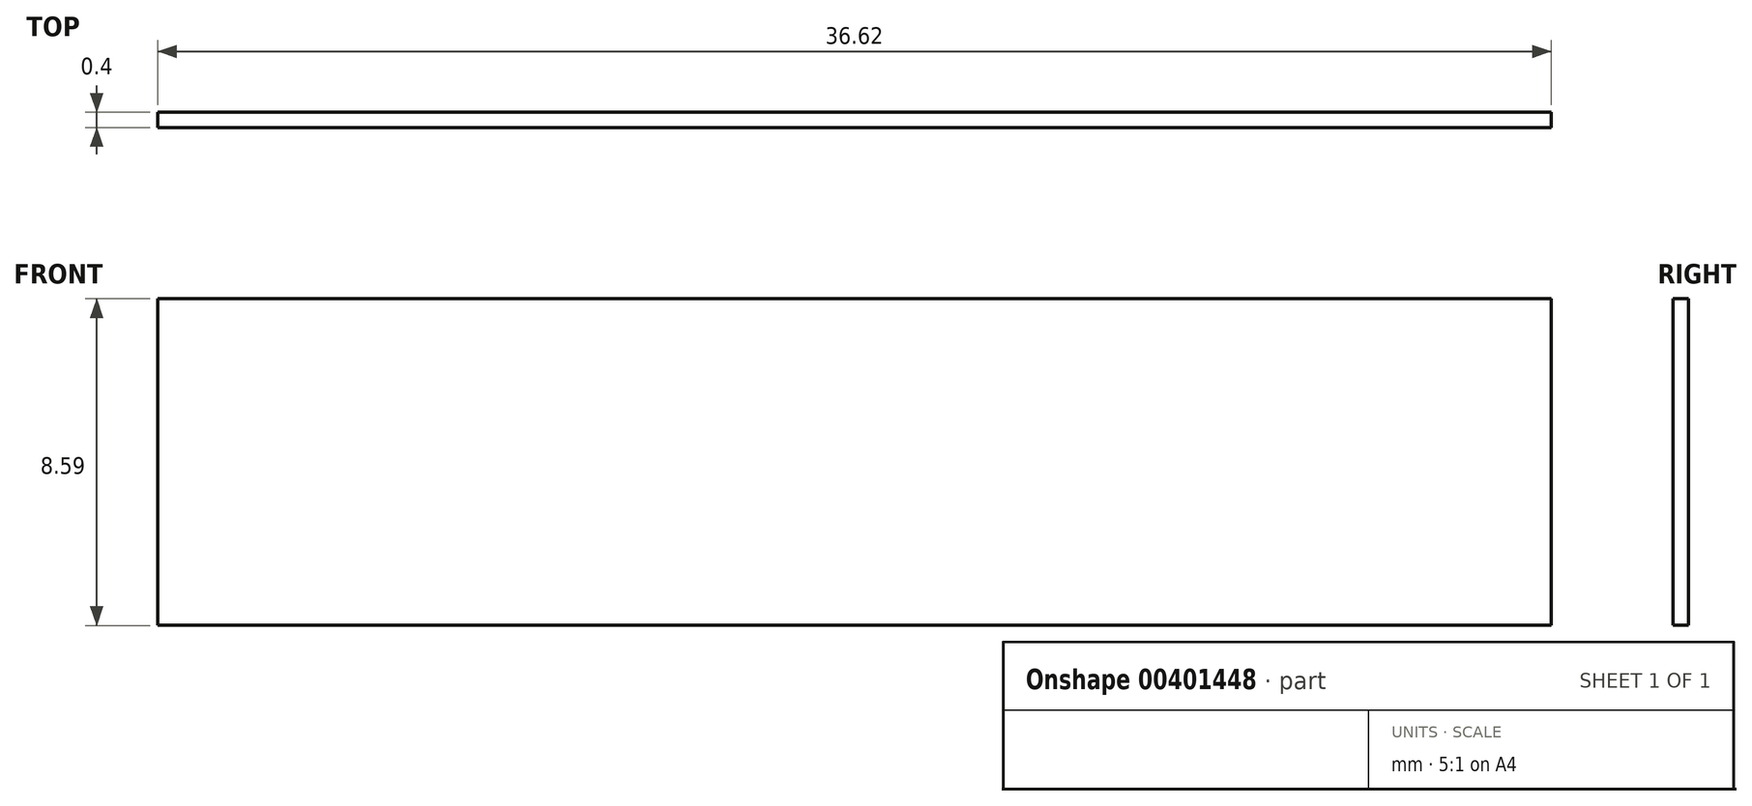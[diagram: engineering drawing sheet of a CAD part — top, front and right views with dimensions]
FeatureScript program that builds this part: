
annotation { "Feature Type Name" : "Feature", "Feature Type Description" : "" }
export const myFeature = defineFeature(function(context is Context, id is Id, definition is map)
    precondition{}
    {
        {
            var Q0;
            Q0=qCreatedBy(makeId("Front.planeOp"),FACE);
            var sketch = newSketch(context, id + "F0", { "sketchPlane" : qUnion([Q0])});
            skLineSegment(sketch, "E0.bottom", {"start": v(-96.57, 56.74) * mm, "end": v(-45.77, 56.74) * mm});
            skLineSegment(sketch, "E0.top", {"start": v(-96.57, 36.3) * mm, "end": v(-45.77, 36.3) * mm});
            skLineSegment(sketch, "E0.left", {"start": v(-96.57, 56.74) * mm, "end": v(-96.57, 36.3) * mm});
            skLineSegment(sketch, "E0.right", {"start": v(-45.77, 56.74) * mm, "end": v(-45.77, 36.3) * mm});
            skSolve(sketch);
        }
        {
            var Q0;
            Q0=makeQuery(id+"F0.imprint","IMPRINT",FACE,{"disambiguationData":[TD([[makeQuery(id+"F0.imprint","IMPRINT",EDGE,{"derivedFrom":sQuery(id+"F0.wireOp",EDGE,"E0.bottom")}),-1.0]])]});
            extrude(context, id + "F1", {"entities" : qUnion([Q0]), "depth" : 1.42 * mm});
        }
        {
            var Q0;
            Q0=qCreatedBy(makeId("Front.planeOp"),FACE);
            var sketch = newSketch(context, id + "F2", { "sketchPlane" : qUnion([Q0])});
            skLineSegment(sketch, "E1.bottom", {"start": v(-111.71, 21.03) * mm, "end": v(-52.05, 21.03) * mm});
            skLineSegment(sketch, "E1.top", {"start": v(-111.71, 5.53) * mm, "end": v(-52.05, 5.53) * mm});
            skLineSegment(sketch, "E1.left", {"start": v(-111.71, 21.03) * mm, "end": v(-111.71, 5.53) * mm});
            skLineSegment(sketch, "E1.right", {"start": v(-52.05, 21.03) * mm, "end": v(-52.05, 5.53) * mm});
            skLineSegment(sketch, "E2.bottom", {"start": v(-110.8, 20.06) * mm, "end": v(-53.17, 20.06) * mm});
            skLineSegment(sketch, "E2.top", {"start": v(-110.8, 6.7) * mm, "end": v(-53.17, 6.7) * mm});
            skLineSegment(sketch, "E2.left", {"start": v(-110.8, 20.06) * mm, "end": v(-110.8, 6.7) * mm});
            skLineSegment(sketch, "E2.right", {"start": v(-53.17, 20.06) * mm, "end": v(-53.17, 6.7) * mm});
            skSolve(sketch);
        }
        {
            var Q0;
            Q0=makeQuery(id+"F2.imprint","IMPRINT",FACE,{"disambiguationData":[TD([[makeQuery(id+"F2.imprint","IMPRINT",EDGE,{"derivedFrom":sQuery(id+"F2.wireOp",EDGE,"E1.bottom")}),-1.0]])]});
            extrude(context, id + "F3", {"entities" : qUnion([Q0]), "depth" : 25.4 * mm});
        }
        {
            var Q0;
            Q0=makeQuery(id+"F3.opExtrude","SWEPT_BODY",BODY,{"disambiguationData":[OSD([sQuery(id+"F2.wireOp",EDGE,"E1.bottom"),sQuery(id+"F2.wireOp",EDGE,"E1.top"),sQuery(id+"F2.wireOp",EDGE,"E1.left"),sQuery(id+"F2.wireOp",EDGE,"E1.right"),sQuery(id+"F2.wireOp",EDGE,"E2.bottom"),sQuery(id+"F2.wireOp",EDGE,"E2.top"),sQuery(id+"F2.wireOp",EDGE,"E2.left"),sQuery(id+"F2.wireOp",EDGE,"E2.right")])]});
            deleteBodies(context, id + "F4", {"entities" : qUnion([Q0])});
        }
        {
            var Q0;
            Q0=makeQuery(id+"F1.opExtrude","SWEPT_BODY",BODY,{"disambiguationData":[OSD([sQuery(id+"F0.wireOp",EDGE,"E0.bottom"),sQuery(id+"F0.wireOp",EDGE,"E0.top"),sQuery(id+"F0.wireOp",EDGE,"E0.left"),sQuery(id+"F0.wireOp",EDGE,"E0.right")])]});
            deleteBodies(context, id + "F5", {"entities" : qUnion([Q0])});
        }
        {
            var Q0;
            Q0=qCreatedBy(makeId("Front.planeOp"),FACE);
            var sketch = newSketch(context, id + "F6", { "sketchPlane" : qUnion([Q0])});
            skLineSegment(sketch, "E3.bottom", {"start": v(-67.27, 42.81) * mm, "end": v(-30.65, 42.81) * mm});
            skLineSegment(sketch, "E3.top", {"start": v(-67.27, 28.38) * mm, "end": v(-30.65, 28.38) * mm});
            skLineSegment(sketch, "E3.left", {"start": v(-67.27, 42.81) * mm, "end": v(-67.27, 28.38) * mm});
            skLineSegment(sketch, "E3.right", {"start": v(-30.65, 42.81) * mm, "end": v(-30.65, 28.38) * mm});
            skSolve(sketch);
        }
        {
            var Q0;
            Q0 = qSketchRegion(id + "F6", true);
            extrude(context, id + "F7", {"entities" : qUnion([Q0]), "depth" : 3.8 * mm});
        }
        {
            var Q0;
            Q0=makeQuery(id+"F7.opExtrude","CAP_FACE",FACE,{"disambiguationData":[OSD([sQuery(id+"F6.wireOp",EDGE,"E3.bottom"),sQuery(id+"F6.wireOp",EDGE,"E3.top"),sQuery(id+"F6.wireOp",EDGE,"E3.left"),sQuery(id+"F6.wireOp",EDGE,"E3.right")])],"isStart":false});
            extrude(context, id + "F8", {"entities" : qUnion([Q0]), "operationType" : NewBodyOperationType.ADD, "depth" : 10.4 * mm});
        }
        {
            var Q0;
            {var subQ0=sQuery(id+"F6.wireOp",EDGE,"E3.bottom");Q0=makeQuery(id+"F8.boolean.opBoolean","MERGE",FACE,{"derivedFrom":[makeQuery(id+"F7.opExtrude","SWEPT_FACE",FACE,{"disambiguationData":[OSD([subQ0])]}),makeQuery(id+"F8.opExtrude","SWEPT_FACE",FACE,{"disambiguationData":[OSD([subQ0])]})]});}
            var sketch = newSketch(context, id + "F9", { "sketchPlane" : qUnion([Q0])});
            skSolve(sketch);
        }
        {
            var Q0;
            Q0 = qSketchRegion(id + "F9", true);
            var Q1;
            {var subQ0=sQuery(id+"F6.wireOp",EDGE,"E3.bottom");Q1=makeQuery(id+"F9.imprint","IMPRINT",FACE,{"disambiguationData":[TD([[makeQuery(id+"F9.imprint","IMPRINT",EDGE,{"derivedFrom":makeQuery(id+"F7.opExtrude","CAP_EDGE",EDGE,{"disambiguationData":[OSD([subQ0])],"isStart":true})}),-1.0]])]});}
            extrude(context, id + "F10", {"entities" : qUnion([Q0, Q1]), "operationType" : NewBodyOperationType.REMOVE, "oppositeDirection" : true, "depth" : 5.08 * mm, "hasSecondDirection" : true, "secondDirectionOppositeDirection" : false, "secondDirectionDepth" : 25.4 * mm});
        }
        {
            var Q0;
            Q0=makeQuery(id+"F8.opExtrude","CAP_FACE",FACE,{"disambiguationData":[OSD([sQuery(id+"F6.wireOp",EDGE,"E3.bottom"),sQuery(id+"F6.wireOp",EDGE,"E3.top"),sQuery(id+"F6.wireOp",EDGE,"E3.left"),sQuery(id+"F6.wireOp",EDGE,"E3.right")])],"isStart":false});
            extrude(context, id + "F11", {"entities" : qUnion([Q0]), "operationType" : NewBodyOperationType.REMOVE, "oppositeDirection" : true, "depth" : 6.1 * mm});
        }
        {
            var Q0;
            Q0=makeQuery(id+"F10.boolean.opBoolean","COPY",FACE,{"derivedFrom":makeQuery(id+"F10.opExtrude","CAP_FACE",FACE,{"disambiguationData":[OSD([sQuery(id+"F6.wireOp",EDGE,"E3.bottom"),sQuery(id+"F6.wireOp",EDGE,"E3.left"),sQuery(id+"F6.wireOp",EDGE,"E3.right")])],"isStart":false})});
            extrude(context, id + "F12", {"entities" : qUnion([Q0]), "operationType" : NewBodyOperationType.REMOVE, "oppositeDirection" : true, "depth" : 3.8 * mm});
        }
        {
            var Q0;
            Q0=makeQuery(id+"F7.opExtrude","CAP_FACE",FACE,{"disambiguationData":[OSD([sQuery(id+"F6.wireOp",EDGE,"E3.bottom"),sQuery(id+"F6.wireOp",EDGE,"E3.top"),sQuery(id+"F6.wireOp",EDGE,"E3.left"),sQuery(id+"F6.wireOp",EDGE,"E3.right")])],"isStart":true});
            extrude(context, id + "F13", {"entities" : qUnion([Q0]), "operationType" : NewBodyOperationType.ADD, "depth" : 9.14 * mm});
        }
        {
            var Q0;
            {var subQ0=sQuery(id+"F6.wireOp",EDGE,"E3.bottom");Q0=makeQuery(id+"F13.boolean.opBoolean","MERGE",FACE,{"derivedFrom":[makeQuery(id+"F12.boolean.opBoolean","COPY",FACE,{"derivedFrom":makeQuery(id+"F12.opExtrude","CAP_FACE",FACE,{"disambiguationData":[OSD([subQ0,sQuery(id+"F6.wireOp",EDGE,"E3.left"),sQuery(id+"F6.wireOp",EDGE,"E3.right")])],"isStart":false})}),makeQuery(id+"F13.opExtrude","SWEPT_FACE",FACE,{"disambiguationData":[OSD([subQ0])]})]});}
            extrude(context, id + "F14", {"entities" : qUnion([Q0]), "operationType" : NewBodyOperationType.ADD, "depth" : 8.38 * mm});
        }
        {
            var Q0;
            {var subQ0=sQuery(id+"F6.wireOp",EDGE,"E3.bottom");Q0=makeQuery(id+"F14.boolean.opBoolean","MERGE",FACE,{"derivedFrom":[makeQuery(id+"F13.opExtrude","CAP_FACE",FACE,{"disambiguationData":[OSD([subQ0,sQuery(id+"F6.wireOp",EDGE,"E3.top"),sQuery(id+"F6.wireOp",EDGE,"E3.left"),sQuery(id+"F6.wireOp",EDGE,"E3.right")])],"isStart":false}),makeQuery(id+"F14.opExtrude","SWEPT_FACE",FACE,{"disambiguationData":[OSD([subQ0]),TDD([makeQuery(id+"F13.opExtrude","CAP_EDGE",EDGE,{"disambiguationData":[OSD([subQ0])],"isStart":false})])]})]});}
            extrude(context, id + "F15", {"entities" : qUnion([Q0]), "operationType" : NewBodyOperationType.REMOVE, "oppositeDirection" : true, "depth" : 4.32 * mm});
        }
        {
            var Q0;
            Q0=makeQuery(id+"F15.boolean.opBoolean","COPY",FACE,{"derivedFrom":makeQuery(id+"F15.opExtrude","CAP_FACE",FACE,{"disambiguationData":[OSD([sQuery(id+"F6.wireOp",EDGE,"E3.bottom"),sQuery(id+"F6.wireOp",EDGE,"E3.top"),sQuery(id+"F6.wireOp",EDGE,"E3.left"),sQuery(id+"F6.wireOp",EDGE,"E3.right")])],"isStart":false})});
            extrude(context, id + "F16", {"entities" : qUnion([Q0]), "operationType" : NewBodyOperationType.REMOVE, "oppositeDirection" : true, "depth" : 5.08 * mm});
        }
        {
            var Q0;
            Q0=makeQuery(id+"F16.boolean.opBoolean","COPY",FACE,{"derivedFrom":makeQuery(id+"F16.opExtrude","CAP_FACE",FACE,{"disambiguationData":[OSD([sQuery(id+"F6.wireOp",EDGE,"E3.bottom"),sQuery(id+"F6.wireOp",EDGE,"E3.top"),sQuery(id+"F6.wireOp",EDGE,"E3.left"),sQuery(id+"F6.wireOp",EDGE,"E3.right")])],"isStart":false})});
            extrude(context, id + "F17", {"entities" : qUnion([Q0]), "operationType" : NewBodyOperationType.REMOVE, "oppositeDirection" : true, "depth" : 2.03 * mm});
        }
        {
            var Q0;
            Q0=makeQuery(id+"F14.opExtrude","CAP_FACE",FACE,{"disambiguationData":[OSD([sQuery(id+"F6.wireOp",EDGE,"E3.bottom"),sQuery(id+"F6.wireOp",EDGE,"E3.left"),sQuery(id+"F6.wireOp",EDGE,"E3.right")])],"isStart":false});
            extrude(context, id + "F18", {"entities" : qUnion([Q0]), "operationType" : NewBodyOperationType.REMOVE, "oppositeDirection" : true, "depth" : 5.33 * mm});
        }
        {
            var Q0;
            Q0=makeQuery(id+"F17.boolean.opBoolean","COPY",FACE,{"derivedFrom":makeQuery(id+"F17.opExtrude","CAP_FACE",FACE,{"disambiguationData":[OSD([sQuery(id+"F6.wireOp",EDGE,"E3.bottom"),sQuery(id+"F6.wireOp",EDGE,"E3.top"),sQuery(id+"F6.wireOp",EDGE,"E3.left"),sQuery(id+"F6.wireOp",EDGE,"E3.right")])],"isStart":false})});
            extrude(context, id + "F19", {"entities" : qUnion([Q0]), "operationType" : NewBodyOperationType.REMOVE, "oppositeDirection" : true, "depth" : 3.3 * mm});
        }
        {
            var Q0;
            {var subQ0=sQuery(id+"F6.wireOp",EDGE,"E3.bottom");Q0=makeQuery(id+"F14.boolean.opBoolean","MERGE",FACE,{"derivedFrom":[makeQuery(id+"F11.boolean.opBoolean","COPY",FACE,{"derivedFrom":makeQuery(id+"F11.opExtrude","CAP_FACE",FACE,{"disambiguationData":[OSD([subQ0,sQuery(id+"F6.wireOp",EDGE,"E3.top"),sQuery(id+"F6.wireOp",EDGE,"E3.left"),sQuery(id+"F6.wireOp",EDGE,"E3.right")])],"isStart":false})}),makeQuery(id+"F14.opExtrude","SWEPT_FACE",FACE,{"disambiguationData":[OSD([subQ0]),TDD([makeQuery(id+"F12.boolean.opBoolean","COPY",EDGE,{"derivedFrom":makeQuery(id+"F12.opExtrude","CAP_EDGE",EDGE,{"disambiguationData":[OSD([subQ0]),TDD([makeQuery(id+"F11.boolean.opBoolean","COPY",EDGE,{"derivedFrom":makeQuery(id+"F11.opExtrude","CAP_EDGE",EDGE,{"disambiguationData":[OSD([subQ0])],"isStart":false})})])],"isStart":false})})])]})]});}
            extrude(context, id + "F20", {"entities" : qUnion([Q0]), "operationType" : NewBodyOperationType.REMOVE, "oppositeDirection" : true, "depth" : 1.04 * mm});
        }
        {
            var Q0;
            Q0=makeQuery(id+"F20.boolean.opBoolean","COPY",FACE,{"derivedFrom":makeQuery(id+"F20.opExtrude","CAP_FACE",FACE,{"disambiguationData":[OSD([sQuery(id+"F6.wireOp",EDGE,"E3.bottom"),sQuery(id+"F6.wireOp",EDGE,"E3.top"),sQuery(id+"F6.wireOp",EDGE,"E3.left"),sQuery(id+"F6.wireOp",EDGE,"E3.right")])],"isStart":false})});
            extrude(context, id + "F21", {"entities" : qUnion([Q0]), "operationType" : NewBodyOperationType.REMOVE, "oppositeDirection" : true, "depth" : 1.1 * mm});
        }
    });
